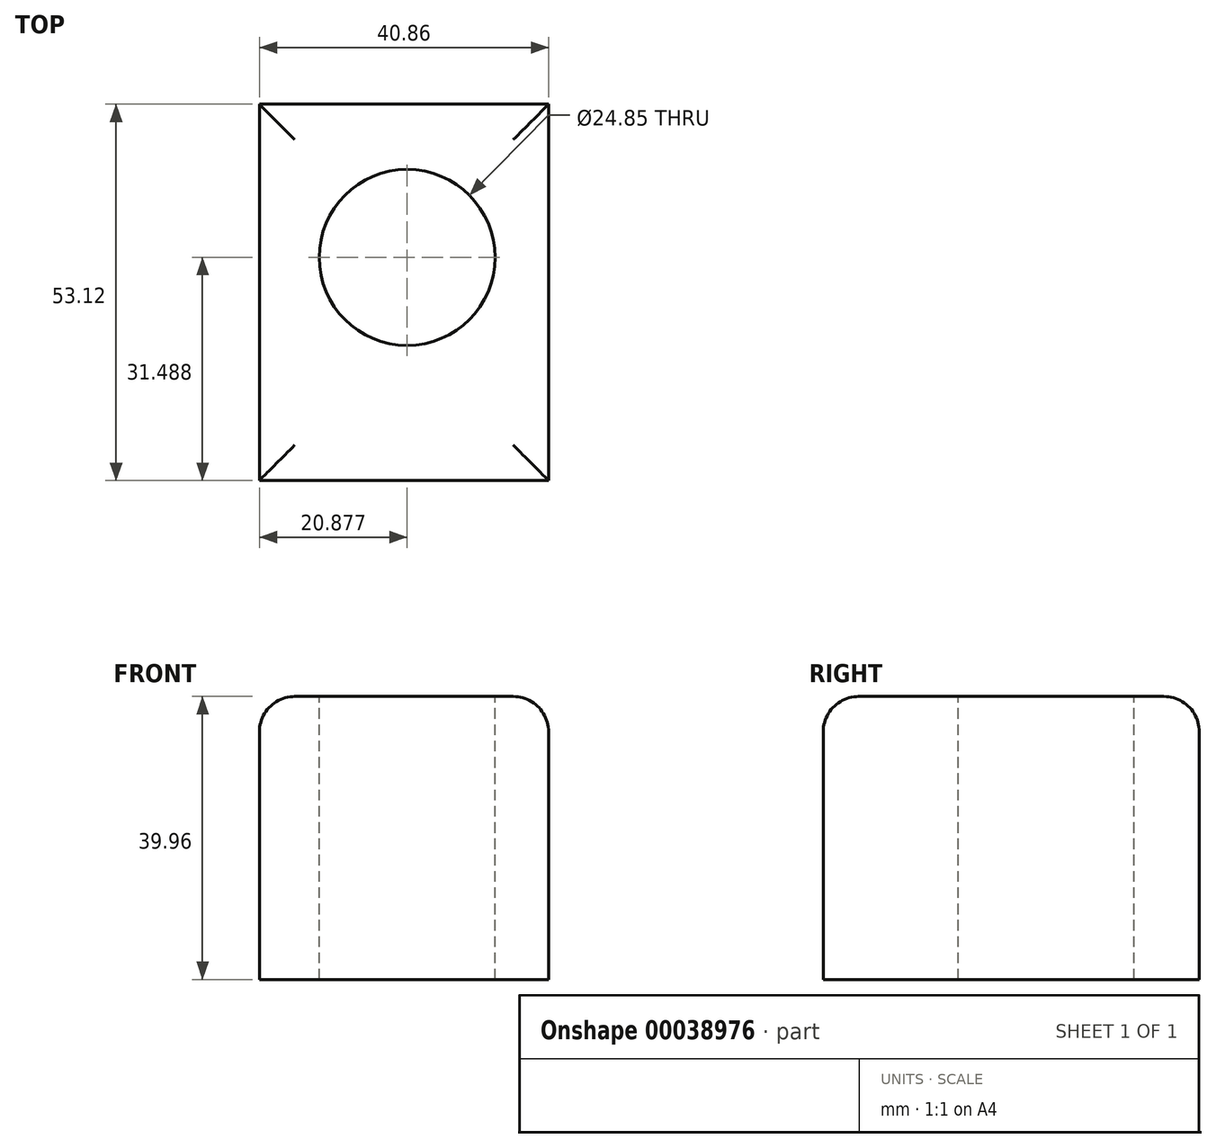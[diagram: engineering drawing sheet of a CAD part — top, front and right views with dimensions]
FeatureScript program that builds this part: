
annotation { "Feature Type Name" : "Feature", "Feature Type Description" : "" }
export const myFeature = defineFeature(function(context is Context, id is Id, definition is map)
    precondition{}
    {
        {
            var Q0;
            Q0=qCreatedBy(makeId("Front.planeOp"),FACE);
            var sketch = newSketch(context, id + "F0", { "sketchPlane" : qUnion([Q0])});
            skLineSegment(sketch, "E0.bottom", {"start": v(45.22, 54.13) * mm, "end": v(4.36, 54.13) * mm});
            skLineSegment(sketch, "E0.top", {"start": v(45.22, 14.17) * mm, "end": v(4.36, 14.17) * mm});
            skLineSegment(sketch, "E0.left", {"start": v(45.22, 54.13) * mm, "end": v(45.22, 14.17) * mm});
            skLineSegment(sketch, "E0.right", {"start": v(4.36, 54.13) * mm, "end": v(4.36, 14.17) * mm});
            skSolve(sketch);
        }
        {
            var Q0;
            Q0=makeQuery(id+"F0.imprint","IMPRINT",FACE,{"disambiguationData":[TD([[makeQuery(id+"F0.imprint","IMPRINT",EDGE,{"derivedFrom":sQuery(id+"F0.wireOp",EDGE,"E0.bottom")}),1.0]])]});
            extrude(context, id + "F1", {"entities" : qUnion([Q0]), "depth" : 53.12 * mm});
        }
        {
            var Q0;
            Q0=makeQuery(id+"F1.opExtrude","SWEPT_FACE",FACE,{"disambiguationData":[OSD([sQuery(id+"F0.wireOp",EDGE,"E0.bottom")])]});
            fillet(context, id + "F2", {"entities" : qUnion([Q0]), "radius" : 5 * mm, "tangentPropagation" : true, "allowEdgeOverflow" : false});
        }
        {
            var Q0;
            Q0=makeQuery(id+"F1.opExtrude","SWEPT_FACE",FACE,{"disambiguationData":[OSD([sQuery(id+"F0.wireOp",EDGE,"E0.bottom")])]});
            var sketch = newSketch(context, id + "F3", { "sketchPlane" : qUnion([Q0])});
            skCircle(sketch, "E1", {"center": v(25.24, -21.63) * mm, "radius": 12.42 * mm});
            skSolve(sketch);
        }
        {
            var Q0;
            Q0 = qSketchRegion(id + "F3", true);
            extrude(context, id + "F4", {"entities" : qUnion([Q0]), "operationType" : NewBodyOperationType.REMOVE, "endBound" : BoundingType.THROUGH_ALL, "oppositeDirection" : true, "depth" : 25 * mm});
        }
    });
